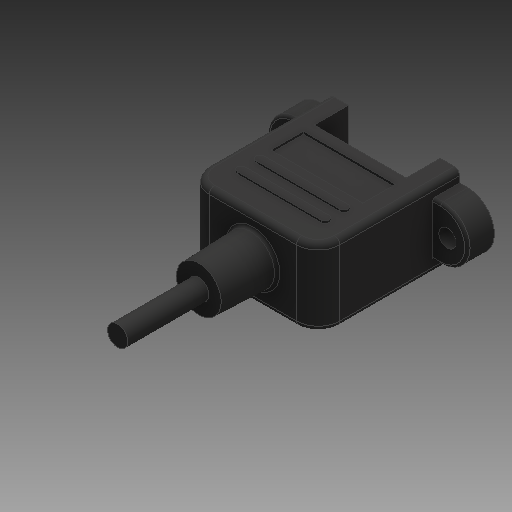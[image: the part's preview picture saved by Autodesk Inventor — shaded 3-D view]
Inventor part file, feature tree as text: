
AUTODESK INVENTOR PART (.ipt)
format: ipt  version: 2019 (Build 230136000, 136)  size: 309,760 bytes
history: native  units: mm
features: sketch x11, extrude x9, fillet x3, mirror x2, plane x1
ambient origin geometry x8: Origin, YZ Plane, XZ Plane, XY Plane, X Axis, Y Axis, Z Axis, Center Point
bodies: Solid1 (feature_tree)
feature tree (26):
  extrude  "Extrusion1"  Depth=26.15mm
  extrude  "Extrusion2"  Depth=14.2mm TaperAngle=0.0deg
  sketch  "Sketch3"  dims[d5=9.9mm d6=6.45mm]
  extrude  "Extrusion3"  Depth=9.9mm
  mirror  "Mirror1"
  extrude  "Extrusion4"  Depth=5.5mm
  extrude  "Extrusion5"  Depth=5.0mm TaperAngle=0.0deg
  extrude  "Extrusion6"  Depth=6.3mm TaperAngle=0.0deg
  sketch  "Sketch8"  dims[d19=10.0mm d20=-0.349066mm d21=3.76mm d22=15.0mm d23=0.0mm d24=12.12mm]
  fillet  "Fillet1"  Radius=9.0mm
  extrude  "Extrusion7"  Depth=12.075mm
  extrude  "Extrusion8"  Depth=15.0mm
  plane  "Work Plane1"
  mirror  "Mirror2"
  fillet  "Fillet2"  Radius=15.0mm
  fillet  "Fillet3"  Radius=12.12mm
  extrude  "Extrusion9"  Depth=1.0mm
  sketch  "Sketch1"  dims[d0=24.15mm d1=26.15mm]
  sketch  "Sketch2"  dims[d2=4.0mm d3=14.2mm d4=0.0mm]
  sketch  "Sketch4"  dims[d7=5.0mm d8=0.0mm d9=5.5mm]
  sketch  "Sketch5"  dims[d10=3.2mm d11=5.0mm d12=0.0mm]
  sketch  "Sketch6"  dims[d13=17.0mm d14=6.3mm d15=0.0mm d16=9.0mm]
  sketch  "Sketch7"  dims[d17=7.1mm d18=12.075mm]
  sketch  "Sketch9"  dims[d25=11.05mm d26=1.0mm]
  sketch  "Sketch10"  dims[d27=17.0mm]
  sketch  "Sketch11"  dims[d28=6.0mm d29=2.0mm d30=0.5mm d31=0.0mm d32=17.0mm d33=1.5mm d34=2.0mm d35=17.0mm d36=1.5mm d37=2.0mm d38=0.75mm d39=0.4mm d40=0.0mm d41=0.5mm d42=0.5mm d43=9.0mm d44=9.0mm d45=4.0mm d46=0.0mm]
